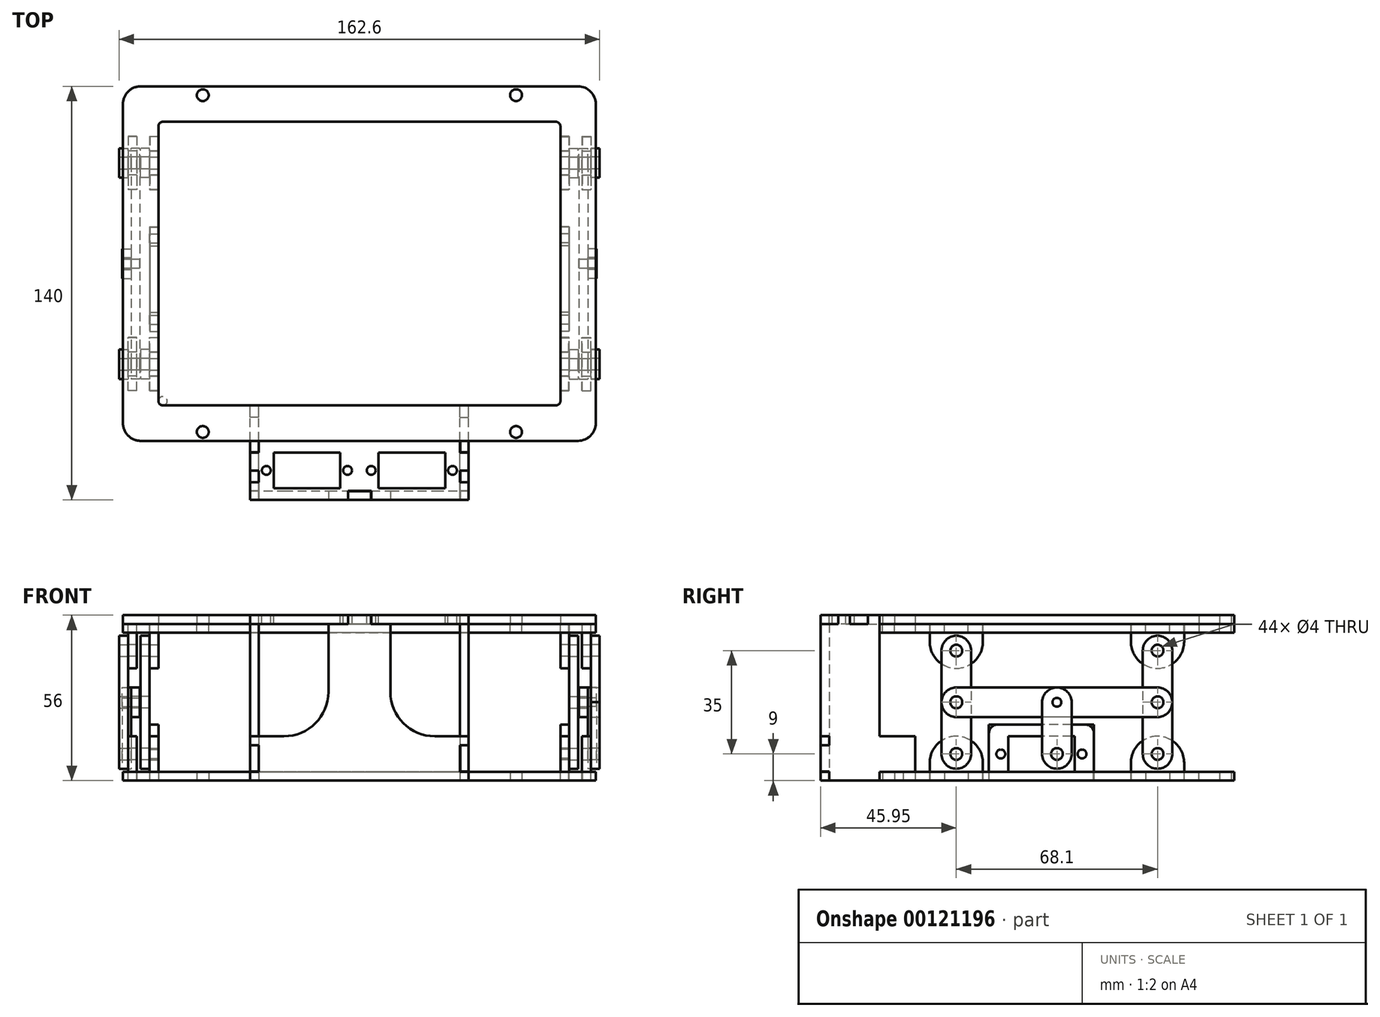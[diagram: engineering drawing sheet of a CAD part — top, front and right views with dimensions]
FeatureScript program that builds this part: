
annotation { "Feature Type Name" : "Feature", "Feature Type Description" : "" }
export const myFeature = defineFeature(function(context is Context, id is Id, definition is map)
    precondition{}
    {
        {
            var Q0;
            Q0=qCreatedBy(makeId("Top.planeOp"),FACE);
            var sketch = newSketch(context, id + "F0", { "sketchPlane" : qUnion([Q0])});
            skLineSegment(sketch, "E0.0.0", {"start": v(-163.03, 1.88) * mm, "end": v(-163.03, -118.12) * mm});
            skLineSegment(sketch, "E0.0.2", {"start": v(-163.03, -118.12) * mm, "end": v(-3.03, -118.12) * mm});
            skLineSegment(sketch, "E0.0.4", {"start": v(-3.03, -118.12) * mm, "end": v(-3.03, 1.88) * mm});
            skLineSegment(sketch, "E0.0.6", {"start": v(-3.03, 1.88) * mm, "end": v(-163.03, 1.88) * mm});
            skLineSegment(sketch, "E1.0", {"start": v(-151.03, -106.12) * mm, "end": v(-151.03, -10.12) * mm});
            skLineSegment(sketch, "E2.0", {"start": v(-151.03, -10.12) * mm, "end": v(-15.03, -10.12) * mm});
            skLineSegment(sketch, "E3.0", {"start": v(-15.03, -10.12) * mm, "end": v(-15.03, -106.12) * mm});
            skLineSegment(sketch, "E4.0", {"start": v(-15.03, -106.12) * mm, "end": v(-151.03, -106.12) * mm});
            skSolve(sketch);
        }
        {
            var Q0;
            Q0=qSketchRegion(id+"F0",true);
            extrude(context, id + "F1", {"entities" : qUnion([Q0]), "depth" : 3 * mm});
        }
        {
            var Q0;
            Q0=makeQuery(id+"F1.opExtrude","SWEPT_EDGE",EDGE,{"disambiguationData":[OSD([sQuery(id+"F0.wireOp",EDGE,"E0.0.0"),sQuery(id+"F0.wireOp",EDGE,"E0.0.2")])]});
            var Q1;
            Q1=makeQuery(id+"F1.opExtrude","SWEPT_EDGE",EDGE,{"disambiguationData":[OSD([sQuery(id+"F0.wireOp",EDGE,"E0.0.2"),sQuery(id+"F0.wireOp",EDGE,"E0.0.4")])]});
            var Q2;
            Q2=makeQuery(id+"F1.opExtrude","SWEPT_EDGE",EDGE,{"disambiguationData":[OSD([sQuery(id+"F0.wireOp",EDGE,"E0.0.0"),sQuery(id+"F0.wireOp",EDGE,"E0.0.6")])]});
            var Q3;
            Q3=makeQuery(id+"F1.opExtrude","SWEPT_EDGE",EDGE,{"disambiguationData":[OSD([sQuery(id+"F0.wireOp",EDGE,"E0.0.4"),sQuery(id+"F0.wireOp",EDGE,"E0.0.6")])]});
            fillet(context, id + "F2", {"entities" : qUnion([Q0, Q1, Q2, Q3]), "radius" : 6 * mm, "tangentPropagation" : true, "allowEdgeOverflow" : false});
        }
        {
            var Q0;
            Q0=makeQuery(id+"F1.opExtrude","SWEPT_EDGE",EDGE,{"disambiguationData":[OSD([sQuery(id+"F0.wireOp",EDGE,"E1.0"),sQuery(id+"F0.wireOp",EDGE,"E2.0")])]});
            var Q1;
            Q1=makeQuery(id+"F1.opExtrude","SWEPT_EDGE",EDGE,{"disambiguationData":[OSD([sQuery(id+"F0.wireOp",EDGE,"E2.0"),sQuery(id+"F0.wireOp",EDGE,"E3.0")])]});
            var Q2;
            Q2=makeQuery(id+"F1.opExtrude","SWEPT_EDGE",EDGE,{"disambiguationData":[OSD([sQuery(id+"F0.wireOp",EDGE,"E3.0"),sQuery(id+"F0.wireOp",EDGE,"E4.0")])]});
            var Q3;
            Q3=makeQuery(id+"F1.opExtrude","SWEPT_EDGE",EDGE,{"disambiguationData":[OSD([sQuery(id+"F0.wireOp",EDGE,"E1.0"),sQuery(id+"F0.wireOp",EDGE,"E4.0")])]});
            fillet(context, id + "F3", {"entities" : qUnion([Q0, Q1, Q2, Q3]), "radius" : 1.5 * mm, "tangentPropagation" : true, "allowEdgeOverflow" : false});
        }
        {
            var Q0;
            Q0=makeQuery(id+"F1.opExtrude","CAP_FACE",FACE,{"disambiguationData":[OSD([sQuery(id+"F0.wireOp",EDGE,"E0.0.0"),sQuery(id+"F0.wireOp",EDGE,"E0.0.2"),sQuery(id+"F0.wireOp",EDGE,"E0.0.4"),sQuery(id+"F0.wireOp",EDGE,"E0.0.6"),sQuery(id+"F0.wireOp",EDGE,"E1.0"),sQuery(id+"F0.wireOp",EDGE,"E2.0"),sQuery(id+"F0.wireOp",EDGE,"E3.0"),sQuery(id+"F0.wireOp",EDGE,"E4.0")])],"isStart":false});
            var sketch = newSketch(context, id + "F4", { "sketchPlane" : qUnion([Q0])});
            skLineSegment(sketch, "E5.bottom", {"start": v(-136.03, 1.88) * mm, "end": v(-30.03, 1.88) * mm, "construction": true});
            skLineSegment(sketch, "E5.top", {"start": v(-136.03, -118.12) * mm, "end": v(-30.03, -118.12) * mm, "construction": true});
            skLineSegment(sketch, "E5.left", {"start": v(-136.03, 1.88) * mm, "end": v(-136.03, -4.12) * mm, "construction": true});
            skLineSegment(sketch, "E5.right", {"start": v(-30.03, 1.88) * mm, "end": v(-30.03, -4.12) * mm, "construction": true});
            skLineSegment(sketch, "E6.trimOffspring", {"start": v(-136.03, -112.12) * mm, "end": v(-136.03, -118.12) * mm, "construction": true});
            skPoint(sketch, "E7.orphan", {"position": v(-149.53, -10.12) * mm});
            skLineSegment(sketch, "E8.trimOffspring", {"start": v(-30.03, -112.12) * mm, "end": v(-30.03, -118.12) * mm, "construction": true});
            skPoint(sketch, "E9.orphan", {"position": v(-16.53, -10.12) * mm});
            skPoint(sketch, "E10.orphan", {"position": v(-16.53, -106.12) * mm});
            skPoint(sketch, "E11.orphan", {"position": v(-149.53, -106.12) * mm});
            skLineSegment(sketch, "E12", {"start": v(-136.03, -4.12) * mm, "end": v(-30.03, -4.12) * mm, "construction": true});
            skLineSegment(sketch, "E13", {"start": v(-136.03, -112.12) * mm, "end": v(-30.03, -112.12) * mm, "construction": true});
            skPoint(sketch, "E14.0.end.orphan", {"position": v(-30.03, -10.12) * mm});
            skPoint(sketch, "E14.0.start.orphan", {"position": v(-136.03, -10.12) * mm});
            skPoint(sketch, "E15.orphan", {"position": v(-30.03, -106.12) * mm});
            skPoint(sketch, "E16.orphan", {"position": v(-136.03, -106.12) * mm});
            skCircle(sketch, "E17", {"center": v(-136.03, -1.12) * mm, "radius": 2 * mm});
            skCircle(sketch, "E18", {"center": v(-30.03, -1.12) * mm, "radius": 2 * mm});
            skCircle(sketch, "E19", {"center": v(-30.03, -115.12) * mm, "radius": 2 * mm});
            skCircle(sketch, "E20", {"center": v(-136.03, -115.12) * mm, "radius": 2 * mm});
            skSolve(sketch);
        }
        {
            var Q0;
            Q0=qSketchRegion(id+"F4",true);
            extrude(context, id + "F5", {"entities" : qUnion([Q0]), "operationType" : NewBodyOperationType.REMOVE, "endBound" : BoundingType.THROUGH_ALL, "oppositeDirection" : true, "depth" : 25 * mm});
        }
        {
            var Q0;
            Q0=makeQuery(id+"F1.opExtrude","CAP_FACE",FACE,{"disambiguationData":[OSD([sQuery(id+"F0.wireOp",EDGE,"E0.0.0"),sQuery(id+"F0.wireOp",EDGE,"E0.0.2"),sQuery(id+"F0.wireOp",EDGE,"E0.0.4"),sQuery(id+"F0.wireOp",EDGE,"E0.0.6"),sQuery(id+"F0.wireOp",EDGE,"E1.0"),sQuery(id+"F0.wireOp",EDGE,"E2.0"),sQuery(id+"F0.wireOp",EDGE,"E3.0"),sQuery(id+"F0.wireOp",EDGE,"E4.0")])],"isStart":false});
            var sketch = newSketch(context, id + "F6", { "sketchPlane" : qUnion([Q0])});
            skLineSegment(sketch, "E21.bottom", {"start": v(-151.03, -101.12) * mm, "end": v(-153.93, -101.12) * mm});
            skLineSegment(sketch, "E21.top", {"start": v(-151.03, -96.22) * mm, "end": v(-153.93, -96.22) * mm});
            skLineSegment(sketch, "E21.left", {"start": v(-151.03, -101.12) * mm, "end": v(-151.03, -96.22) * mm});
            skLineSegment(sketch, "E21.right", {"start": v(-153.93, -101.12) * mm, "end": v(-153.93, -96.22) * mm});
            skLineSegment(sketch, "E22.bottom", {"start": v(-151.03, -88.12) * mm, "end": v(-153.93, -88.12) * mm});
            skLineSegment(sketch, "E22.top", {"start": v(-151.03, -83.22) * mm, "end": v(-153.93, -83.22) * mm});
            skLineSegment(sketch, "E22.left", {"start": v(-151.03, -88.12) * mm, "end": v(-151.03, -83.22) * mm});
            skLineSegment(sketch, "E22.right", {"start": v(-153.93, -88.12) * mm, "end": v(-153.93, -83.22) * mm});
            skLineSegment(sketch, "E23.bottom", {"start": v(-158.43, -101.12) * mm, "end": v(-161.33, -101.12) * mm});
            skLineSegment(sketch, "E23.top", {"start": v(-158.43, -96.22) * mm, "end": v(-161.33, -96.22) * mm});
            skLineSegment(sketch, "E23.left", {"start": v(-158.43, -101.12) * mm, "end": v(-158.43, -96.22) * mm});
            skLineSegment(sketch, "E23.right", {"start": v(-161.33, -101.12) * mm, "end": v(-161.33, -96.22) * mm});
            skLineSegment(sketch, "E24.bottom", {"start": v(-158.43, -88.12) * mm, "end": v(-161.33, -88.12) * mm});
            skLineSegment(sketch, "E24.top", {"start": v(-158.43, -83.22) * mm, "end": v(-161.33, -83.22) * mm});
            skLineSegment(sketch, "E24.left", {"start": v(-158.43, -88.12) * mm, "end": v(-158.43, -83.22) * mm});
            skLineSegment(sketch, "E24.right", {"start": v(-161.33, -88.12) * mm, "end": v(-161.33, -83.22) * mm});
            skLineSegment(sketch, "E25", {"start": v(-163.03, -58.12) * mm, "end": v(-3.03, -58.12) * mm, "construction": true});
            skLineSegment(sketch, "E26", {"start": v(-83.03, 1.88) * mm, "end": v(-83.03, -118.12) * mm, "construction": true});
            skLineSegment(sketch, "E27.MirrorCS", {"start": v(-4.73, -101.12) * mm, "end": v(-4.73, -96.22) * mm});
            skLineSegment(sketch, "E28.MirrorCS", {"start": v(-7.63, -101.12) * mm, "end": v(-7.63, -96.22) * mm});
            skLineSegment(sketch, "E29.MirrorCS", {"start": v(-7.63, -96.22) * mm, "end": v(-4.73, -96.22) * mm});
            skLineSegment(sketch, "E30.MirrorCS", {"start": v(-7.63, -88.12) * mm, "end": v(-4.73, -88.12) * mm});
            skLineSegment(sketch, "E31.MirrorCS", {"start": v(-7.63, -101.12) * mm, "end": v(-4.73, -101.12) * mm});
            skLineSegment(sketch, "E32.MirrorCS", {"start": v(-12.13, -88.12) * mm, "end": v(-12.13, -83.22) * mm});
            skLineSegment(sketch, "E33.MirrorCS", {"start": v(-15.03, -88.12) * mm, "end": v(-15.03, -83.22) * mm});
            skLineSegment(sketch, "E34.MirrorCS", {"start": v(-15.03, -83.22) * mm, "end": v(-12.13, -83.22) * mm});
            skLineSegment(sketch, "E35.MirrorCS", {"start": v(-15.03, -88.12) * mm, "end": v(-12.13, -88.12) * mm});
            skLineSegment(sketch, "E36.MirrorCS", {"start": v(-12.13, -101.12) * mm, "end": v(-12.13, -96.22) * mm});
            skLineSegment(sketch, "E37.MirrorCS", {"start": v(-15.03, -101.12) * mm, "end": v(-15.03, -96.22) * mm});
            skLineSegment(sketch, "E38.MirrorCS", {"start": v(-7.63, -83.22) * mm, "end": v(-4.73, -83.22) * mm});
            skLineSegment(sketch, "E39.MirrorCS", {"start": v(-7.63, -88.12) * mm, "end": v(-7.63, -83.22) * mm});
            skLineSegment(sketch, "E40.MirrorCS", {"start": v(-15.03, -96.22) * mm, "end": v(-12.13, -96.22) * mm});
            skLineSegment(sketch, "E41.MirrorCS", {"start": v(-15.03, -101.12) * mm, "end": v(-12.13, -101.12) * mm});
            skLineSegment(sketch, "E42.MirrorCS", {"start": v(-4.73, -88.12) * mm, "end": v(-4.73, -83.22) * mm});
            skLineSegment(sketch, "E43.MirrorCS", {"start": v(-7.63, -15.12) * mm, "end": v(-4.73, -15.12) * mm});
            skLineSegment(sketch, "E44.MirrorCS", {"start": v(-153.93, -15.12) * mm, "end": v(-153.93, -20.02) * mm});
            skLineSegment(sketch, "E45.MirrorCS", {"start": v(-15.03, -20.02) * mm, "end": v(-12.13, -20.02) * mm});
            skLineSegment(sketch, "E46.MirrorCS", {"start": v(-161.33, -28.12) * mm, "end": v(-161.33, -33.02) * mm});
            skLineSegment(sketch, "E47.MirrorCS", {"start": v(-158.43, -20.02) * mm, "end": v(-161.33, -20.02) * mm});
            skLineSegment(sketch, "E48.MirrorCS", {"start": v(-15.03, -33.02) * mm, "end": v(-12.13, -33.02) * mm});
            skLineSegment(sketch, "E49.MirrorCS", {"start": v(-15.03, -28.12) * mm, "end": v(-12.13, -28.12) * mm});
            skLineSegment(sketch, "E50.MirrorCS", {"start": v(-158.43, -15.12) * mm, "end": v(-158.43, -20.02) * mm});
            skLineSegment(sketch, "E51.MirrorCS", {"start": v(-15.03, -15.12) * mm, "end": v(-15.03, -20.02) * mm});
            skLineSegment(sketch, "E52.MirrorCS", {"start": v(-4.73, -15.12) * mm, "end": v(-4.73, -20.02) * mm});
            skLineSegment(sketch, "E53.MirrorCS", {"start": v(-7.63, -15.12) * mm, "end": v(-7.63, -20.02) * mm});
            skLineSegment(sketch, "E54.MirrorCS", {"start": v(-151.03, -15.12) * mm, "end": v(-151.03, -20.02) * mm});
            skLineSegment(sketch, "E55.MirrorCS", {"start": v(-151.03, -15.12) * mm, "end": v(-153.93, -15.12) * mm});
            skLineSegment(sketch, "E56.MirrorCS", {"start": v(-15.03, -15.12) * mm, "end": v(-12.13, -15.12) * mm});
            skLineSegment(sketch, "E57.MirrorCS", {"start": v(-158.43, -15.12) * mm, "end": v(-161.33, -15.12) * mm});
            skLineSegment(sketch, "E58.MirrorCS", {"start": v(-12.13, -15.12) * mm, "end": v(-12.13, -20.02) * mm});
            skLineSegment(sketch, "E59.MirrorCS", {"start": v(-7.63, -33.02) * mm, "end": v(-4.73, -33.02) * mm});
            skLineSegment(sketch, "E60.MirrorCS", {"start": v(-153.93, -28.12) * mm, "end": v(-153.93, -33.02) * mm});
            skLineSegment(sketch, "E61.MirrorCS", {"start": v(-158.43, -28.12) * mm, "end": v(-158.43, -33.02) * mm});
            skLineSegment(sketch, "E62.MirrorCS", {"start": v(-15.03, -28.12) * mm, "end": v(-15.03, -33.02) * mm});
            skLineSegment(sketch, "E63.MirrorCS", {"start": v(-151.03, -33.02) * mm, "end": v(-153.93, -33.02) * mm});
            skLineSegment(sketch, "E64.MirrorCS", {"start": v(-151.03, -20.02) * mm, "end": v(-153.93, -20.02) * mm});
            skLineSegment(sketch, "E65.MirrorCS", {"start": v(-7.63, -20.02) * mm, "end": v(-4.73, -20.02) * mm});
            skLineSegment(sketch, "E66.MirrorCS", {"start": v(-7.63, -28.12) * mm, "end": v(-7.63, -33.02) * mm});
            skLineSegment(sketch, "E67.MirrorCS", {"start": v(-158.43, -28.12) * mm, "end": v(-161.33, -28.12) * mm});
            skLineSegment(sketch, "E68.MirrorCS", {"start": v(-4.73, -28.12) * mm, "end": v(-4.73, -33.02) * mm});
            skLineSegment(sketch, "E69.MirrorCS", {"start": v(-151.03, -28.12) * mm, "end": v(-153.93, -28.12) * mm});
            skLineSegment(sketch, "E70.MirrorCS", {"start": v(-151.03, -28.12) * mm, "end": v(-151.03, -33.02) * mm});
            skLineSegment(sketch, "E71.MirrorCS", {"start": v(-7.63, -28.12) * mm, "end": v(-4.73, -28.12) * mm});
            skLineSegment(sketch, "E72.MirrorCS", {"start": v(-158.43, -33.02) * mm, "end": v(-161.33, -33.02) * mm});
            skLineSegment(sketch, "E73.MirrorCS", {"start": v(-12.13, -28.12) * mm, "end": v(-12.13, -33.02) * mm});
            skLineSegment(sketch, "E74.MirrorCS", {"start": v(-161.33, -15.12) * mm, "end": v(-161.33, -20.02) * mm});
            skSolve(sketch);
        }
        {
            var Q0;
            Q0 = qSketchRegion(id + "F6", true);
            extrude(context, id + "F7", {"entities" : qUnion([Q0]), "operationType" : NewBodyOperationType.REMOVE, "endBound" : BoundingType.THROUGH_ALL, "oppositeDirection" : true, "depth" : 25 * mm});
        }
        {
            var Q0;
            Q0=makeQuery(id+"F1.opExtrude","CAP_FACE",FACE,{"disambiguationData":[OSD([sQuery(id+"F0.wireOp",EDGE,"E0.0.0"),sQuery(id+"F0.wireOp",EDGE,"E0.0.2"),sQuery(id+"F0.wireOp",EDGE,"E0.0.4"),sQuery(id+"F0.wireOp",EDGE,"E0.0.6"),sQuery(id+"F0.wireOp",EDGE,"E1.0"),sQuery(id+"F0.wireOp",EDGE,"E2.0"),sQuery(id+"F0.wireOp",EDGE,"E3.0"),sQuery(id+"F0.wireOp",EDGE,"E4.0")])],"isStart":false});
            var sketch = newSketch(context, id + "F8", { "sketchPlane" : qUnion([Q0])});
            skLineSegment(sketch, "E75.0", {"start": v(-9.03, 1.88) * mm, "end": v(-157.03, 1.88) * mm});
            skLineSegment(sketch, "E76.0", {"start": v(-163.03, -4.12) * mm, "end": v(-163.03, -112.12) * mm});
            skArc(sketch, "E77.0.1", {"start": v(-157.03, 1.88) * mm, "mid": v(-161.28, 0.12) * mm, "end": v(-163.03, -4.12) * mm});
            skArc(sketch, "E77.0.3", {"start": v(-163.03, -112.12) * mm, "mid": v(-161.28, -116.36) * mm, "end": v(-157.03, -118.12) * mm});
            skLineSegment(sketch, "E77.0.4", {"start": v(-157.03, -118.12) * mm, "end": v(-9.03, -118.12) * mm});
            skArc(sketch, "E77.0.5", {"start": v(-9.03, -118.12) * mm, "mid": v(-4.8, -116.36) * mm, "end": v(-3.03, -112.12) * mm});
            skLineSegment(sketch, "E77.0.6", {"start": v(-3.03, -112.12) * mm, "end": v(-3.03, -4.12) * mm});
            skArc(sketch, "E77.0.7", {"start": v(-3.03, -4.12) * mm, "mid": v(-4.8, 0.12) * mm, "end": v(-9.03, 1.88) * mm});
            skArc(sketch, "E78.0", {"start": v(-149.53, -106.12) * mm, "mid": v(-150.6, -105.68) * mm, "end": v(-151.03, -104.62) * mm});
            skLineSegment(sketch, "E79.0", {"start": v(-16.53, -106.12) * mm, "end": v(-149.53, -106.12) * mm});
            skArc(sketch, "E80.0", {"start": v(-151.03, -11.62) * mm, "mid": v(-150.6, -10.56) * mm, "end": v(-149.53, -10.12) * mm});
            skLineSegment(sketch, "E81.0", {"start": v(-149.53, -10.12) * mm, "end": v(-16.53, -10.12) * mm});
            skArc(sketch, "E82.0", {"start": v(-16.53, -10.12) * mm, "mid": v(-15.47, -10.56) * mm, "end": v(-15.03, -11.62) * mm});
            skArc(sketch, "E83.0", {"start": v(-15.03, -104.62) * mm, "mid": v(-15.47, -105.68) * mm, "end": v(-16.53, -106.12) * mm});
            skCircle(sketch, "E84.0", {"center": v(-30.03, -1.12) * mm, "radius": 2 * mm});
            skCircle(sketch, "E85.0", {"center": v(-136.03, -1.12) * mm, "radius": 2 * mm});
            skCircle(sketch, "E86.0", {"center": v(-30.03, -115.12) * mm, "radius": 2 * mm});
            skCircle(sketch, "E87.0", {"center": v(-136.03, -115.12) * mm, "radius": 2 * mm});
            skLineSegment(sketch, "E88", {"start": v(-151.03, -11.62) * mm, "end": v(-151.03, -104.62) * mm});
            skLineSegment(sketch, "E89", {"start": v(-15.03, -11.62) * mm, "end": v(-15.03, -104.62) * mm});
            skSolve(sketch);
        }
        {
            var Q0;
            Q0 = qSketchRegion(id + "F8", true);
            extrude(context, id + "F9", {"entities" : qUnion([Q0]), "depth" : 3 * mm});
        }
        {
            var Q0;
            {var subQ3=sQuery(id+"F0.wireOp",EDGE,"E1.0");Q0=makeQuery(id+"F7.boolean.opBoolean","SPLIT",FACE,{"disambiguationData":[TD([makeQuery(id+"F7.opExtrude","SWEPT_FACE",FACE,{"disambiguationData":[OSD([sQuery(id+"F6.wireOp",EDGE,"E21.top")])]})])],"derivedFrom":makeQuery(id+"F1.opExtrude","SWEPT_FACE",FACE,{"disambiguationData":[OSD([subQ3])]})});}
            var sketch = newSketch(context, id + "F10", { "sketchPlane" : qUnion([Q0])});
            skLineSegment(sketch, "E90.bottom", {"start": v(-101.17, 3) * mm, "end": v(-96.17, 3) * mm});
            skLineSegment(sketch, "E90.left", {"start": v(-101.17, 3) * mm, "end": v(-101.17, -3) * mm});
            skLineSegment(sketch, "E90.right", {"start": v(-83.17, 3) * mm, "end": v(-83.17, -3) * mm});
            skLineSegment(sketch, "E91.top", {"start": v(-96.17, 0) * mm, "end": v(-88.17, 0) * mm});
            skLineSegment(sketch, "E91.left", {"start": v(-96.17, 3) * mm, "end": v(-96.17, 0) * mm});
            skLineSegment(sketch, "E91.right", {"start": v(-88.17, 3) * mm, "end": v(-88.17, 0) * mm});
            skLineSegment(sketch, "E92", {"start": v(-92.17, 0) * mm, "end": v(-92.17, -12) * mm, "construction": true});
            skCircle(sketch, "E93", {"center": v(-92.17, -6) * mm, "radius": 2 * mm});
            skArc(sketch, "E94", {"start": v(-101.17, -3) * mm, "mid": v(-92.17, -12) * mm, "end": v(-83.17, -3) * mm});
            skPoint(sketch, "E94.first.point", {"position": v(-101.17, -3) * mm});
            skPoint(sketch, "E94.second.point", {"position": v(-83.17, -3) * mm});
            skPoint(sketch, "E94.third.point", {"position": v(-92.17, -12) * mm});
            skLineSegment(sketch, "E95.trimOffspring", {"start": v(-88.17, 3) * mm, "end": v(-83.17, 3) * mm});
            skLineSegment(sketch, "E96", {"start": v(-92.17, 3) * mm, "end": v(-92.17, 0) * mm, "construction": true});
            skSolve(sketch);
        }
        {
            var Q0;
            {var subQ8=sQuery(id+"F10.wireOp",EDGE,"E90.left");Q0=makeQuery(id+"F10.imprint","IMPRINT",FACE,{"disambiguationData":[TD([[makeQuery(id+"F10.imprint","IMPRINT",EDGE,{"derivedFrom":subQ8}),1.0]])]});}
            extrude(context, id + "F11", {"entities" : qUnion([Q0]), "oppositeDirection" : true, "depth" : 3 * mm});
        }
        {
            var Q0;
            {var subQ3=sQuery(id+"F0.wireOp",EDGE,"E1.0");Q0=makeQuery(id+"F7.boolean.opBoolean","SPLIT",FACE,{"disambiguationData":[TD([makeQuery(id+"F7.opExtrude","SWEPT_FACE",FACE,{"disambiguationData":[OSD([sQuery(id+"F6.wireOp",EDGE,"E22.top")])]})])],"derivedFrom":makeQuery(id+"F1.opExtrude","SWEPT_FACE",FACE,{"disambiguationData":[OSD([subQ3])]})});}
            var Q1;
            Q1=makeQuery(id+"F7.boolean.opBoolean","COPY",FACE,{"derivedFrom":makeQuery(id+"F7.opExtrude","SWEPT_FACE",FACE,{"disambiguationData":[OSD([sQuery(id+"F6.wireOp",EDGE,"E24.right")])]})});
            cPlane(context, id + "F12", {"entities" : qUnion([Q0, Q1]), "cplaneType" : CPlaneType.MID_PLANE, "offset" : 25 * mm, "width" : 150 * mm, "height" : 150 * mm});
        }
        {
            var Q0;
            Q0=makeQuery(id+"F11.opExtrude","SWEPT_BODY",BODY,{"disambiguationData":[OSD([sQuery(id+"F0.wireOp",EDGE,"E1.0"),sQuery(id+"F6.wireOp",EDGE,"E21.top"),sQuery(id+"F6.wireOp",EDGE,"E22.bottom"),sQuery(id+"F6.wireOp",EDGE,"E21.left"),sQuery(id+"F6.wireOp",EDGE,"E22.left"),sQuery(id+"F10.wireOp",EDGE,"E90.bottom"),sQuery(id+"F10.wireOp",EDGE,"E90.left"),sQuery(id+"F10.wireOp",EDGE,"E90.right"),sQuery(id+"F10.wireOp",EDGE,"E91.top"),sQuery(id+"F10.wireOp",EDGE,"E93"),sQuery(id+"F10.wireOp",EDGE,"E94"),sQuery(id+"F10.wireOp",EDGE,"E95.trimOffspring")])]});
            var Q1;
            Q1=qCreatedBy(id+"F12.planeOp",FACE);
            mirror(context, id + "F13", {"entities" : qUnion([Q0]), "mirrorPlane" : qUnion([Q1])});
        }
        {
            var Q0;
            Q0=makeQuery(id+"F1.opExtrude","SWEPT_FACE",FACE,{"disambiguationData":[OSD([sQuery(id+"F0.wireOp",EDGE,"E0.0.4")])]});
            var Q1;
            Q1=makeQuery(id+"F1.opExtrude","SWEPT_FACE",FACE,{"disambiguationData":[OSD([sQuery(id+"F0.wireOp",EDGE,"E0.0.0")])]});
            cPlane(context, id + "F14", {"entities" : qUnion([Q0, Q1]), "cplaneType" : CPlaneType.MID_PLANE, "offset" : 25 * mm, "width" : 150 * mm, "height" : 150 * mm});
        }
        {
            var Q0;
            Q0=makeQuery(id+"F1.opExtrude","SWEPT_FACE",FACE,{"disambiguationData":[OSD([sQuery(id+"F0.wireOp",EDGE,"E0.0.2")])]});
            var Q1;
            Q1=makeQuery(id+"F1.opExtrude","SWEPT_FACE",FACE,{"disambiguationData":[OSD([sQuery(id+"F0.wireOp",EDGE,"E0.0.6")])]});
            cPlane(context, id + "F15", {"entities" : qUnion([Q0, Q1]), "cplaneType" : CPlaneType.MID_PLANE, "offset" : 25 * mm, "width" : 150 * mm, "height" : 150 * mm});
        }
        {
            var Q0;
            Q0=makeQuery(id+"F11.opExtrude","SWEPT_BODY",BODY,{"disambiguationData":[OSD([sQuery(id+"F0.wireOp",EDGE,"E1.0"),sQuery(id+"F6.wireOp",EDGE,"E21.top"),sQuery(id+"F6.wireOp",EDGE,"E22.bottom"),sQuery(id+"F6.wireOp",EDGE,"E21.left"),sQuery(id+"F6.wireOp",EDGE,"E22.left"),sQuery(id+"F10.wireOp",EDGE,"E90.bottom"),sQuery(id+"F10.wireOp",EDGE,"E90.left"),sQuery(id+"F10.wireOp",EDGE,"E90.right"),sQuery(id+"F10.wireOp",EDGE,"E91.top"),sQuery(id+"F10.wireOp",EDGE,"E93"),sQuery(id+"F10.wireOp",EDGE,"E94"),sQuery(id+"F10.wireOp",EDGE,"E95.trimOffspring")])]});
            var Q1;
            Q1=makeQuery(id+"F13.opPattern","COPY",BODY,{"derivedFrom":makeQuery(id+"F11.opExtrude","SWEPT_BODY",BODY,{"disambiguationData":[OSD([sQuery(id+"F0.wireOp",EDGE,"E1.0"),sQuery(id+"F6.wireOp",EDGE,"E21.top"),sQuery(id+"F6.wireOp",EDGE,"E22.bottom"),sQuery(id+"F6.wireOp",EDGE,"E21.left"),sQuery(id+"F6.wireOp",EDGE,"E22.left"),sQuery(id+"F10.wireOp",EDGE,"E90.bottom"),sQuery(id+"F10.wireOp",EDGE,"E90.left"),sQuery(id+"F10.wireOp",EDGE,"E90.right"),sQuery(id+"F10.wireOp",EDGE,"E91.top"),sQuery(id+"F10.wireOp",EDGE,"E93"),sQuery(id+"F10.wireOp",EDGE,"E94"),sQuery(id+"F10.wireOp",EDGE,"E95.trimOffspring")])]}),"instanceName":"1"});
            var Q2;
            Q2=qCreatedBy(id+"F14.planeOp",FACE);
            mirror(context, id + "F16", {"entities" : qUnion([Q0, Q1]), "mirrorPlane" : qUnion([Q2])});
        }
        {
            var Q0;
            Q0=makeQuery(id+"F11.opExtrude","SWEPT_BODY",BODY,{"disambiguationData":[OSD([sQuery(id+"F0.wireOp",EDGE,"E1.0"),sQuery(id+"F6.wireOp",EDGE,"E21.top"),sQuery(id+"F6.wireOp",EDGE,"E22.bottom"),sQuery(id+"F6.wireOp",EDGE,"E21.left"),sQuery(id+"F6.wireOp",EDGE,"E22.left"),sQuery(id+"F10.wireOp",EDGE,"E90.bottom"),sQuery(id+"F10.wireOp",EDGE,"E90.left"),sQuery(id+"F10.wireOp",EDGE,"E90.right"),sQuery(id+"F10.wireOp",EDGE,"E91.top"),sQuery(id+"F10.wireOp",EDGE,"E93"),sQuery(id+"F10.wireOp",EDGE,"E94"),sQuery(id+"F10.wireOp",EDGE,"E95.trimOffspring")])]});
            var Q1;
            Q1=makeQuery(id+"F13.opPattern","COPY",BODY,{"derivedFrom":makeQuery(id+"F11.opExtrude","SWEPT_BODY",BODY,{"disambiguationData":[OSD([sQuery(id+"F0.wireOp",EDGE,"E1.0"),sQuery(id+"F6.wireOp",EDGE,"E21.top"),sQuery(id+"F6.wireOp",EDGE,"E22.bottom"),sQuery(id+"F6.wireOp",EDGE,"E21.left"),sQuery(id+"F6.wireOp",EDGE,"E22.left"),sQuery(id+"F10.wireOp",EDGE,"E90.bottom"),sQuery(id+"F10.wireOp",EDGE,"E90.left"),sQuery(id+"F10.wireOp",EDGE,"E90.right"),sQuery(id+"F10.wireOp",EDGE,"E91.top"),sQuery(id+"F10.wireOp",EDGE,"E93"),sQuery(id+"F10.wireOp",EDGE,"E94"),sQuery(id+"F10.wireOp",EDGE,"E95.trimOffspring")])]}),"instanceName":"1"});
            var Q2;
            Q2=makeQuery(id+"F16.opPattern","COPY",BODY,{"derivedFrom":makeQuery(id+"F11.opExtrude","SWEPT_BODY",BODY,{"disambiguationData":[OSD([sQuery(id+"F0.wireOp",EDGE,"E1.0"),sQuery(id+"F6.wireOp",EDGE,"E21.top"),sQuery(id+"F6.wireOp",EDGE,"E22.bottom"),sQuery(id+"F6.wireOp",EDGE,"E21.left"),sQuery(id+"F6.wireOp",EDGE,"E22.left"),sQuery(id+"F10.wireOp",EDGE,"E90.bottom"),sQuery(id+"F10.wireOp",EDGE,"E90.left"),sQuery(id+"F10.wireOp",EDGE,"E90.right"),sQuery(id+"F10.wireOp",EDGE,"E91.top"),sQuery(id+"F10.wireOp",EDGE,"E93"),sQuery(id+"F10.wireOp",EDGE,"E94"),sQuery(id+"F10.wireOp",EDGE,"E95.trimOffspring")])]}),"instanceName":"1"});
            var Q3;
            Q3=makeQuery(id+"F16.opPattern","COPY",BODY,{"derivedFrom":makeQuery(id+"F13.opPattern","COPY",BODY,{"derivedFrom":makeQuery(id+"F11.opExtrude","SWEPT_BODY",BODY,{"disambiguationData":[OSD([sQuery(id+"F0.wireOp",EDGE,"E1.0"),sQuery(id+"F6.wireOp",EDGE,"E21.top"),sQuery(id+"F6.wireOp",EDGE,"E22.bottom"),sQuery(id+"F6.wireOp",EDGE,"E21.left"),sQuery(id+"F6.wireOp",EDGE,"E22.left"),sQuery(id+"F10.wireOp",EDGE,"E90.bottom"),sQuery(id+"F10.wireOp",EDGE,"E90.left"),sQuery(id+"F10.wireOp",EDGE,"E90.right"),sQuery(id+"F10.wireOp",EDGE,"E91.top"),sQuery(id+"F10.wireOp",EDGE,"E93"),sQuery(id+"F10.wireOp",EDGE,"E94"),sQuery(id+"F10.wireOp",EDGE,"E95.trimOffspring")])]}),"instanceName":"1"}),"instanceName":"1"});
            var Q4;
            Q4=qCreatedBy(id+"F15.planeOp",FACE);
            mirror(context, id + "F17", {"entities" : qUnion([Q0, Q1, Q2, Q3]), "mirrorPlane" : qUnion([Q4])});
        }
        {
            var Q0;
            Q0=makeQuery(id+"F16.opPattern","COPY",FACE,{"derivedFrom":makeQuery(id+"F13.opPattern","COPY",FACE,{"derivedFrom":makeQuery(id+"F11.opExtrude","CAP_FACE",FACE,{"disambiguationData":[OSD([sQuery(id+"F0.wireOp",EDGE,"E1.0"),sQuery(id+"F6.wireOp",EDGE,"E21.top"),sQuery(id+"F6.wireOp",EDGE,"E22.bottom"),sQuery(id+"F6.wireOp",EDGE,"E21.left"),sQuery(id+"F6.wireOp",EDGE,"E22.left"),sQuery(id+"F10.wireOp",EDGE,"E90.bottom"),sQuery(id+"F10.wireOp",EDGE,"E90.left"),sQuery(id+"F10.wireOp",EDGE,"E90.right"),sQuery(id+"F10.wireOp",EDGE,"E91.top"),sQuery(id+"F10.wireOp",EDGE,"E93"),sQuery(id+"F10.wireOp",EDGE,"E94"),sQuery(id+"F10.wireOp",EDGE,"E95.trimOffspring")])],"isStart":true}),"instanceName":"1"}),"instanceName":"1"});
            var sketch = newSketch(context, id + "F18", { "sketchPlane" : qUnion([Q0])});
            skArc(sketch, "E97", {"start": v(-87.17, -6) * mm, "mid": v(-92.17, -1) * mm, "end": v(-97.17, -6) * mm});
            skCircle(sketch, "E98", {"center": v(-92.17, -6) * mm, "radius": 2 * mm});
            skLineSegment(sketch, "E99", {"start": v(-92.17, -6) * mm, "end": v(-92.17, -41) * mm, "construction": true});
            skLineSegment(sketch, "E100", {"start": v(-87.17, -6) * mm, "end": v(-87.17, -41) * mm});
            skLineSegment(sketch, "E101", {"start": v(-97.17, -6) * mm, "end": v(-97.17, -41) * mm});
            skCircle(sketch, "E102", {"center": v(-92.17, -41) * mm, "radius": 2 * mm});
            skCircle(sketch, "E103", {"center": v(-92.17, -23.5) * mm, "radius": 2 * mm});
            skArc(sketch, "E104", {"start": v(-97.17, -41) * mm, "mid": v(-92.17, -46) * mm, "end": v(-87.17, -41) * mm});
            skSolve(sketch);
        }
        {
            var Q0;
            Q0=makeQuery(id+"F18.imprint","IMPRINT",FACE,{"disambiguationData":[TD([[makeQuery(id+"F18.imprint","IMPRINT",EDGE,{"derivedFrom":sQuery(id+"F18.wireOp",EDGE,"E102")}),-1.0]])]});
            var Q1;
            {var subQ1=sQuery(id+"F18.wireOp",EDGE,"E97");Q1=makeQuery(id+"F18.imprint","IMPRINT",FACE,{"disambiguationData":[TD([[makeQuery(id+"F18.imprint","IMPRINT",EDGE,{"derivedFrom":subQ1}),1.0]])]});}
            extrude(context, id + "F19", {"entities" : qUnion([Q0, Q1]), "depth" : 3 * mm});
        }
        {
            var Q0;
            Q0=makeQuery(id+"F16.opPattern","COPY",FACE,{"derivedFrom":makeQuery(id+"F11.opExtrude","CAP_FACE",FACE,{"disambiguationData":[OSD([sQuery(id+"F0.wireOp",EDGE,"E1.0"),sQuery(id+"F6.wireOp",EDGE,"E21.top"),sQuery(id+"F6.wireOp",EDGE,"E22.bottom"),sQuery(id+"F6.wireOp",EDGE,"E21.left"),sQuery(id+"F6.wireOp",EDGE,"E22.left"),sQuery(id+"F10.wireOp",EDGE,"E90.bottom"),sQuery(id+"F10.wireOp",EDGE,"E90.left"),sQuery(id+"F10.wireOp",EDGE,"E90.right"),sQuery(id+"F10.wireOp",EDGE,"E91.top"),sQuery(id+"F10.wireOp",EDGE,"E93"),sQuery(id+"F10.wireOp",EDGE,"E94"),sQuery(id+"F10.wireOp",EDGE,"E95.trimOffspring")])],"isStart":false}),"instanceName":"1"});
            var Q1;
            Q1=makeQuery(id+"F19.opExtrude","CAP_FACE",FACE,{"disambiguationData":[OSD([sQuery(id+"F18.wireOp",EDGE,"E97"),sQuery(id+"F18.wireOp",EDGE,"E98"),sQuery(id+"F18.wireOp",EDGE,"E100"),sQuery(id+"F18.wireOp",EDGE,"E101"),sQuery(id+"F18.wireOp",EDGE,"E102"),sQuery(id+"F18.wireOp",EDGE,"E103"),sQuery(id+"F18.wireOp",EDGE,"E104")])],"isStart":false});
            cPlane(context, id + "F20", {"entities" : qUnion([Q0, Q1]), "cplaneType" : CPlaneType.MID_PLANE, "offset" : 25 * mm, "width" : 150 * mm, "height" : 150 * mm});
        }
        {
            var Q0;
            Q0=makeQuery(id+"F19.opExtrude","SWEPT_BODY",BODY,{"disambiguationData":[OSD([sQuery(id+"F18.wireOp",EDGE,"E97"),sQuery(id+"F18.wireOp",EDGE,"E98"),sQuery(id+"F18.wireOp",EDGE,"E100"),sQuery(id+"F18.wireOp",EDGE,"E101"),sQuery(id+"F18.wireOp",EDGE,"E102"),sQuery(id+"F18.wireOp",EDGE,"E103"),sQuery(id+"F18.wireOp",EDGE,"E104")])]});
            var Q1;
            Q1=qCreatedBy(id+"F20.planeOp",FACE);
            mirror(context, id + "F21", {"entities" : qUnion([Q0]), "mirrorPlane" : qUnion([Q1])});
        }
        {
            var Q0;
            Q0=makeQuery(id+"F19.opExtrude","SWEPT_BODY",BODY,{"disambiguationData":[OSD([sQuery(id+"F18.wireOp",EDGE,"E97"),sQuery(id+"F18.wireOp",EDGE,"E98"),sQuery(id+"F18.wireOp",EDGE,"E100"),sQuery(id+"F18.wireOp",EDGE,"E101"),sQuery(id+"F18.wireOp",EDGE,"E102"),sQuery(id+"F18.wireOp",EDGE,"E103"),sQuery(id+"F18.wireOp",EDGE,"E104")])]});
            var Q1;
            Q1=makeQuery(id+"F21.opPattern","COPY",BODY,{"derivedFrom":makeQuery(id+"F19.opExtrude","SWEPT_BODY",BODY,{"disambiguationData":[OSD([sQuery(id+"F18.wireOp",EDGE,"E97"),sQuery(id+"F18.wireOp",EDGE,"E98"),sQuery(id+"F18.wireOp",EDGE,"E100"),sQuery(id+"F18.wireOp",EDGE,"E101"),sQuery(id+"F18.wireOp",EDGE,"E102"),sQuery(id+"F18.wireOp",EDGE,"E103"),sQuery(id+"F18.wireOp",EDGE,"E104")])]}),"instanceName":"1"});
            var Q2;
            Q2=qCreatedBy(id+"F14.planeOp",FACE);
            mirror(context, id + "F22", {"entities" : qUnion([Q0, Q1]), "mirrorPlane" : qUnion([Q2])});
        }
        {
            var Q0;
            Q0=makeQuery(id+"F22.opPattern","COPY",BODY,{"derivedFrom":makeQuery(id+"F21.opPattern","COPY",BODY,{"derivedFrom":makeQuery(id+"F19.opExtrude","SWEPT_BODY",BODY,{"disambiguationData":[OSD([sQuery(id+"F18.wireOp",EDGE,"E97"),sQuery(id+"F18.wireOp",EDGE,"E98"),sQuery(id+"F18.wireOp",EDGE,"E100"),sQuery(id+"F18.wireOp",EDGE,"E101"),sQuery(id+"F18.wireOp",EDGE,"E102"),sQuery(id+"F18.wireOp",EDGE,"E103"),sQuery(id+"F18.wireOp",EDGE,"E104")])]}),"instanceName":"1"}),"instanceName":"1"});
            var Q1;
            Q1=makeQuery(id+"F19.opExtrude","SWEPT_BODY",BODY,{"disambiguationData":[OSD([sQuery(id+"F18.wireOp",EDGE,"E97"),sQuery(id+"F18.wireOp",EDGE,"E98"),sQuery(id+"F18.wireOp",EDGE,"E100"),sQuery(id+"F18.wireOp",EDGE,"E101"),sQuery(id+"F18.wireOp",EDGE,"E102"),sQuery(id+"F18.wireOp",EDGE,"E103"),sQuery(id+"F18.wireOp",EDGE,"E104")])]});
            var Q2;
            Q2=makeQuery(id+"F22.opPattern","COPY",BODY,{"derivedFrom":makeQuery(id+"F19.opExtrude","SWEPT_BODY",BODY,{"disambiguationData":[OSD([sQuery(id+"F18.wireOp",EDGE,"E97"),sQuery(id+"F18.wireOp",EDGE,"E98"),sQuery(id+"F18.wireOp",EDGE,"E100"),sQuery(id+"F18.wireOp",EDGE,"E101"),sQuery(id+"F18.wireOp",EDGE,"E102"),sQuery(id+"F18.wireOp",EDGE,"E103"),sQuery(id+"F18.wireOp",EDGE,"E104")])]}),"instanceName":"1"});
            var Q3;
            Q3=makeQuery(id+"F21.opPattern","COPY",BODY,{"derivedFrom":makeQuery(id+"F19.opExtrude","SWEPT_BODY",BODY,{"disambiguationData":[OSD([sQuery(id+"F18.wireOp",EDGE,"E97"),sQuery(id+"F18.wireOp",EDGE,"E98"),sQuery(id+"F18.wireOp",EDGE,"E100"),sQuery(id+"F18.wireOp",EDGE,"E101"),sQuery(id+"F18.wireOp",EDGE,"E102"),sQuery(id+"F18.wireOp",EDGE,"E103"),sQuery(id+"F18.wireOp",EDGE,"E104")])]}),"instanceName":"1"});
            var Q4;
            Q4=qCreatedBy(id+"F15.planeOp",FACE);
            mirror(context, id + "F23", {"entities" : qUnion([Q0, Q1, Q2, Q3]), "mirrorPlane" : qUnion([Q4])});
        }
        {
            var Q0;
            Q0=makeQuery(id+"F19.opExtrude","CAP_FACE",FACE,{"disambiguationData":[OSD([sQuery(id+"F18.wireOp",EDGE,"E97"),sQuery(id+"F18.wireOp",EDGE,"E98"),sQuery(id+"F18.wireOp",EDGE,"E100"),sQuery(id+"F18.wireOp",EDGE,"E101"),sQuery(id+"F18.wireOp",EDGE,"E102"),sQuery(id+"F18.wireOp",EDGE,"E103"),sQuery(id+"F18.wireOp",EDGE,"E104")])],"isStart":false});
            var sketch = newSketch(context, id + "F24", { "sketchPlane" : qUnion([Q0])});
            skCircle(sketch, "E105.0", {"center": v(-24.07, -23.5) * mm, "radius": 2 * mm});
            skLineSegment(sketch, "E106", {"start": v(-24.07, -23.5) * mm, "end": v(-92.17, -23.5) * mm, "construction": true});
            skCircle(sketch, "E107", {"center": v(-92.17, -23.5) * mm, "radius": 2 * mm});
            skArc(sketch, "E108.0.startCap", {"start": v(-24.07, -18.5) * mm, "mid": v(-19.07, -23.5) * mm, "end": v(-24.07, -28.5) * mm});
            skArc(sketch, "E108.0.endCap", {"start": v(-92.17, -28.5) * mm, "mid": v(-97.17, -23.5) * mm, "end": v(-92.17, -18.5) * mm});
            skLineSegment(sketch, "E108.0.left", {"start": v(-24.07, -28.5) * mm, "end": v(-92.17, -28.5) * mm});
            skLineSegment(sketch, "E108.0.right", {"start": v(-24.07, -18.5) * mm, "end": v(-92.17, -18.5) * mm});
            skSolve(sketch);
        }
        {
            var Q0;
            Q0 = qSketchRegion(id + "F24", true);
            extrude(context, id + "F25", {"entities" : qUnion([Q0]), "oppositeDirection" : true, "depth" : 7 * mm});
        }
        {
            var Q0;
            Q0 = qSketchRegion(id + "F24", true);
            extrude(context, id + "F26", {"entities" : qUnion([Q0]), "operationType" : NewBodyOperationType.REMOVE, "oppositeDirection" : true, "depth" : 4 * mm});
        }
        {
            var Q0;
            Q0=makeQuery(id+"F25.opExtrude","SWEPT_BODY",BODY,{"disambiguationData":[OSD([sQuery(id+"F24.wireOp",EDGE,"E105.0"),sQuery(id+"F24.wireOp",EDGE,"E107"),sQuery(id+"F24.wireOp",EDGE,"E108.0.startCap"),sQuery(id+"F24.wireOp",EDGE,"E108.0.endCap"),sQuery(id+"F24.wireOp",EDGE,"E108.0.left"),sQuery(id+"F24.wireOp",EDGE,"E108.0.right")])]});
            var Q1;
            Q1=qCreatedBy(id+"F14.planeOp",FACE);
            mirror(context, id + "F27", {"entities" : qUnion([Q0]), "mirrorPlane" : qUnion([Q1])});
        }
        {
            var Q0;
            Q0=makeQuery(id+"F27.opPattern","COPY",FACE,{"derivedFrom":makeQuery(id+"F25.opExtrude","SWEPT_FACE",FACE,{"disambiguationData":[OSD([sQuery(id+"F24.wireOp",EDGE,"E108.0.right")])]}),"instanceName":"1"});
            var Q1;
            Q1=makeQuery(id+"F27.opPattern","COPY",FACE,{"derivedFrom":makeQuery(id+"F25.opExtrude","SWEPT_FACE",FACE,{"disambiguationData":[OSD([sQuery(id+"F24.wireOp",EDGE,"E108.0.left")])]}),"instanceName":"1"});
            cPlane(context, id + "F28", {"entities" : qUnion([Q0, Q1]), "cplaneType" : CPlaneType.MID_PLANE, "offset" : 25 * mm, "width" : 150 * mm, "height" : 150 * mm});
        }
        {
            var Q0;
            Q0=makeQuery(id+"F17.opPattern","COPY",BODY,{"derivedFrom":makeQuery(id+"F13.opPattern","COPY",BODY,{"derivedFrom":makeQuery(id+"F11.opExtrude","SWEPT_BODY",BODY,{"disambiguationData":[OSD([sQuery(id+"F0.wireOp",EDGE,"E1.0"),sQuery(id+"F6.wireOp",EDGE,"E21.top"),sQuery(id+"F6.wireOp",EDGE,"E22.bottom"),sQuery(id+"F6.wireOp",EDGE,"E21.left"),sQuery(id+"F6.wireOp",EDGE,"E22.left"),sQuery(id+"F10.wireOp",EDGE,"E90.bottom"),sQuery(id+"F10.wireOp",EDGE,"E90.left"),sQuery(id+"F10.wireOp",EDGE,"E90.right"),sQuery(id+"F10.wireOp",EDGE,"E91.top"),sQuery(id+"F10.wireOp",EDGE,"E93"),sQuery(id+"F10.wireOp",EDGE,"E94"),sQuery(id+"F10.wireOp",EDGE,"E95.trimOffspring")])]}),"instanceName":"1"}),"instanceName":"1"});
            var Q1;
            Q1=makeQuery(id+"F13.opPattern","COPY",BODY,{"derivedFrom":makeQuery(id+"F11.opExtrude","SWEPT_BODY",BODY,{"disambiguationData":[OSD([sQuery(id+"F0.wireOp",EDGE,"E1.0"),sQuery(id+"F6.wireOp",EDGE,"E21.top"),sQuery(id+"F6.wireOp",EDGE,"E22.bottom"),sQuery(id+"F6.wireOp",EDGE,"E21.left"),sQuery(id+"F6.wireOp",EDGE,"E22.left"),sQuery(id+"F10.wireOp",EDGE,"E90.bottom"),sQuery(id+"F10.wireOp",EDGE,"E90.left"),sQuery(id+"F10.wireOp",EDGE,"E90.right"),sQuery(id+"F10.wireOp",EDGE,"E91.top"),sQuery(id+"F10.wireOp",EDGE,"E93"),sQuery(id+"F10.wireOp",EDGE,"E94"),sQuery(id+"F10.wireOp",EDGE,"E95.trimOffspring")])]}),"instanceName":"1"});
            var Q2;
            Q2=makeQuery(id+"F16.opPattern","COPY",BODY,{"derivedFrom":makeQuery(id+"F13.opPattern","COPY",BODY,{"derivedFrom":makeQuery(id+"F11.opExtrude","SWEPT_BODY",BODY,{"disambiguationData":[OSD([sQuery(id+"F0.wireOp",EDGE,"E1.0"),sQuery(id+"F6.wireOp",EDGE,"E21.top"),sQuery(id+"F6.wireOp",EDGE,"E22.bottom"),sQuery(id+"F6.wireOp",EDGE,"E21.left"),sQuery(id+"F6.wireOp",EDGE,"E22.left"),sQuery(id+"F10.wireOp",EDGE,"E90.bottom"),sQuery(id+"F10.wireOp",EDGE,"E90.left"),sQuery(id+"F10.wireOp",EDGE,"E90.right"),sQuery(id+"F10.wireOp",EDGE,"E91.top"),sQuery(id+"F10.wireOp",EDGE,"E93"),sQuery(id+"F10.wireOp",EDGE,"E94"),sQuery(id+"F10.wireOp",EDGE,"E95.trimOffspring")])]}),"instanceName":"1"}),"instanceName":"1"});
            var Q3;
            Q3=makeQuery(id+"F17.opPattern","COPY",BODY,{"derivedFrom":makeQuery(id+"F16.opPattern","COPY",BODY,{"derivedFrom":makeQuery(id+"F13.opPattern","COPY",BODY,{"derivedFrom":makeQuery(id+"F11.opExtrude","SWEPT_BODY",BODY,{"disambiguationData":[OSD([sQuery(id+"F0.wireOp",EDGE,"E1.0"),sQuery(id+"F6.wireOp",EDGE,"E21.top"),sQuery(id+"F6.wireOp",EDGE,"E22.bottom"),sQuery(id+"F6.wireOp",EDGE,"E21.left"),sQuery(id+"F6.wireOp",EDGE,"E22.left"),sQuery(id+"F10.wireOp",EDGE,"E90.bottom"),sQuery(id+"F10.wireOp",EDGE,"E90.left"),sQuery(id+"F10.wireOp",EDGE,"E90.right"),sQuery(id+"F10.wireOp",EDGE,"E91.top"),sQuery(id+"F10.wireOp",EDGE,"E93"),sQuery(id+"F10.wireOp",EDGE,"E94"),sQuery(id+"F10.wireOp",EDGE,"E95.trimOffspring")])]}),"instanceName":"1"}),"instanceName":"1"}),"instanceName":"1"});
            var Q4;
            Q4=makeQuery(id+"F1.opExtrude","SWEPT_BODY",BODY,{"disambiguationData":[OSD([sQuery(id+"F0.wireOp",EDGE,"E0.0.0"),sQuery(id+"F0.wireOp",EDGE,"E0.0.2"),sQuery(id+"F0.wireOp",EDGE,"E0.0.4"),sQuery(id+"F0.wireOp",EDGE,"E0.0.6"),sQuery(id+"F0.wireOp",EDGE,"E1.0"),sQuery(id+"F0.wireOp",EDGE,"E2.0"),sQuery(id+"F0.wireOp",EDGE,"E3.0"),sQuery(id+"F0.wireOp",EDGE,"E4.0")])]});
            var Q5;
            Q5=makeQuery(id+"F11.opExtrude","SWEPT_BODY",BODY,{"disambiguationData":[OSD([sQuery(id+"F0.wireOp",EDGE,"E1.0"),sQuery(id+"F6.wireOp",EDGE,"E21.top"),sQuery(id+"F6.wireOp",EDGE,"E22.bottom"),sQuery(id+"F6.wireOp",EDGE,"E21.left"),sQuery(id+"F6.wireOp",EDGE,"E22.left"),sQuery(id+"F10.wireOp",EDGE,"E90.bottom"),sQuery(id+"F10.wireOp",EDGE,"E90.left"),sQuery(id+"F10.wireOp",EDGE,"E90.right"),sQuery(id+"F10.wireOp",EDGE,"E91.top"),sQuery(id+"F10.wireOp",EDGE,"E93"),sQuery(id+"F10.wireOp",EDGE,"E94"),sQuery(id+"F10.wireOp",EDGE,"E95.trimOffspring")])]});
            var Q6;
            Q6=makeQuery(id+"F17.opPattern","COPY",BODY,{"derivedFrom":makeQuery(id+"F11.opExtrude","SWEPT_BODY",BODY,{"disambiguationData":[OSD([sQuery(id+"F0.wireOp",EDGE,"E1.0"),sQuery(id+"F6.wireOp",EDGE,"E21.top"),sQuery(id+"F6.wireOp",EDGE,"E22.bottom"),sQuery(id+"F6.wireOp",EDGE,"E21.left"),sQuery(id+"F6.wireOp",EDGE,"E22.left"),sQuery(id+"F10.wireOp",EDGE,"E90.bottom"),sQuery(id+"F10.wireOp",EDGE,"E90.left"),sQuery(id+"F10.wireOp",EDGE,"E90.right"),sQuery(id+"F10.wireOp",EDGE,"E91.top"),sQuery(id+"F10.wireOp",EDGE,"E93"),sQuery(id+"F10.wireOp",EDGE,"E94"),sQuery(id+"F10.wireOp",EDGE,"E95.trimOffspring")])]}),"instanceName":"1"});
            var Q7;
            Q7=makeQuery(id+"F17.opPattern","COPY",BODY,{"derivedFrom":makeQuery(id+"F16.opPattern","COPY",BODY,{"derivedFrom":makeQuery(id+"F11.opExtrude","SWEPT_BODY",BODY,{"disambiguationData":[OSD([sQuery(id+"F0.wireOp",EDGE,"E1.0"),sQuery(id+"F6.wireOp",EDGE,"E21.top"),sQuery(id+"F6.wireOp",EDGE,"E22.bottom"),sQuery(id+"F6.wireOp",EDGE,"E21.left"),sQuery(id+"F6.wireOp",EDGE,"E22.left"),sQuery(id+"F10.wireOp",EDGE,"E90.bottom"),sQuery(id+"F10.wireOp",EDGE,"E90.left"),sQuery(id+"F10.wireOp",EDGE,"E90.right"),sQuery(id+"F10.wireOp",EDGE,"E91.top"),sQuery(id+"F10.wireOp",EDGE,"E93"),sQuery(id+"F10.wireOp",EDGE,"E94"),sQuery(id+"F10.wireOp",EDGE,"E95.trimOffspring")])]}),"instanceName":"1"}),"instanceName":"1"});
            var Q8;
            Q8=makeQuery(id+"F16.opPattern","COPY",BODY,{"derivedFrom":makeQuery(id+"F11.opExtrude","SWEPT_BODY",BODY,{"disambiguationData":[OSD([sQuery(id+"F0.wireOp",EDGE,"E1.0"),sQuery(id+"F6.wireOp",EDGE,"E21.top"),sQuery(id+"F6.wireOp",EDGE,"E22.bottom"),sQuery(id+"F6.wireOp",EDGE,"E21.left"),sQuery(id+"F6.wireOp",EDGE,"E22.left"),sQuery(id+"F10.wireOp",EDGE,"E90.bottom"),sQuery(id+"F10.wireOp",EDGE,"E90.left"),sQuery(id+"F10.wireOp",EDGE,"E90.right"),sQuery(id+"F10.wireOp",EDGE,"E91.top"),sQuery(id+"F10.wireOp",EDGE,"E93"),sQuery(id+"F10.wireOp",EDGE,"E94"),sQuery(id+"F10.wireOp",EDGE,"E95.trimOffspring")])]}),"instanceName":"1"});
            var Q9;
            Q9=qCreatedBy(id+"F28.planeOp",FACE);
            mirror(context, id + "F29", {"entities" : qUnion([Q0, Q1, Q2, Q3, Q4, Q5, Q6, Q7, Q8]), "mirrorPlane" : qUnion([Q9])});
        }
        {
            var Q0;
            Q0=makeQuery(id+"F26.boolean.opBoolean","COPY",FACE,{"derivedFrom":makeQuery(id+"F26.opExtrude","CAP_FACE",FACE,{"disambiguationData":[OSD([sQuery(id+"F24.wireOp",EDGE,"E105.0"),sQuery(id+"F24.wireOp",EDGE,"E107"),sQuery(id+"F24.wireOp",EDGE,"E108.0.startCap"),sQuery(id+"F24.wireOp",EDGE,"E108.0.endCap"),sQuery(id+"F24.wireOp",EDGE,"E108.0.left"),sQuery(id+"F24.wireOp",EDGE,"E108.0.right")])],"isStart":false})});
            var sketch = newSketch(context, id + "F30", { "sketchPlane" : qUnion([Q0])});
            skLineSegment(sketch, "E109", {"start": v(-97.17, -23.5) * mm, "end": v(-19.07, -23.5) * mm, "construction": true});
            skCircle(sketch, "E110", {"center": v(-58.12, -23.5) * mm, "radius": 1.5 * mm});
            skSolve(sketch);
        }
        {
            var Q0;
            Q0 = qSketchRegion(id + "F30", true);
            var Q1;
            Q1=makeQuery(id+"F25.opExtrude","SWEPT_BODY",BODY,{"disambiguationData":[OSD([sQuery(id+"F24.wireOp",EDGE,"E105.0"),sQuery(id+"F24.wireOp",EDGE,"E107"),sQuery(id+"F24.wireOp",EDGE,"E108.0.startCap"),sQuery(id+"F24.wireOp",EDGE,"E108.0.endCap"),sQuery(id+"F24.wireOp",EDGE,"E108.0.left"),sQuery(id+"F24.wireOp",EDGE,"E108.0.right")])]});
            extrude(context, id + "F31", {"entities" : qUnion([Q0]), "operationType" : NewBodyOperationType.REMOVE, "endBound" : BoundingType.THROUGH_ALL, "oppositeDirection" : true, "endBoundEntityBody" : qUnion([Q1]), "depth" : 25 * mm});
        }
        {
            var Q0;
            {var subQ1=sQuery(id+"F0.wireOp",EDGE,"E3.0");Q0=makeQuery(id+"F29.opPattern","COPY",FACE,{"derivedFrom":makeQuery(id+"F7.boolean.opBoolean","SPLIT",FACE,{"disambiguationData":[TD([makeQuery(id+"F7.opExtrude","SWEPT_FACE",FACE,{"disambiguationData":[OSD([sQuery(id+"F6.wireOp",EDGE,"E34.MirrorCS")])]})])],"derivedFrom":makeQuery(id+"F1.opExtrude","SWEPT_FACE",FACE,{"disambiguationData":[OSD([subQ1])]})}),"instanceName":"1"});}
            var sketch = newSketch(context, id + "F32", { "sketchPlane" : qUnion([Q0])});
            skLineSegment(sketch, "E111", {"start": v(58.12, -50) * mm, "end": v(58.12, -13.96) * mm, "construction": true});
            skLineSegment(sketch, "E112", {"start": v(49.62, -41) * mm, "end": v(77.12, -41) * mm, "construction": true});
            skLineSegment(sketch, "E113.bottom", {"start": v(52.12, -35) * mm, "end": v(74.62, -35) * mm});
            skLineSegment(sketch, "E113.top", {"start": v(52.12, -47) * mm, "end": v(74.62, -47) * mm});
            skLineSegment(sketch, "E113.left", {"start": v(52.12, -35) * mm, "end": v(52.12, -47) * mm});
            skLineSegment(sketch, "E113.right", {"start": v(74.62, -35) * mm, "end": v(74.62, -47) * mm});
            skCircle(sketch, "E114", {"center": v(49.62, -41) * mm, "radius": 1.5 * mm});
            skCircle(sketch, "E115", {"center": v(77.12, -41) * mm, "radius": 1.5 * mm});
            skCircle(sketch, "E116", {"center": v(58.12, -41) * mm, "radius": 6 * mm, "construction": true});
            skPoint(sketch, "E116.first.point", {"position": v(58.12, -35) * mm});
            skPoint(sketch, "E116.second.point", {"position": v(52.12, -41) * mm});
            skPoint(sketch, "E116.third.point", {"position": v(58.12, -47) * mm});
            skLineSegment(sketch, "E117", {"start": v(58.12, -41) * mm, "end": v(58.12, -35) * mm, "construction": true});
            skLineSegment(sketch, "E118.bottom", {"start": v(45.62, -31) * mm, "end": v(81.12, -31) * mm});
            skLineSegment(sketch, "E118.top", {"start": v(45.62, -50) * mm, "end": v(81.12, -50) * mm});
            skLineSegment(sketch, "E118.left", {"start": v(45.62, -31) * mm, "end": v(45.62, -50) * mm});
            skLineSegment(sketch, "E118.right", {"start": v(81.12, -31) * mm, "end": v(81.12, -50) * mm});
            skSolve(sketch);
        }
        {
            var Q0;
            Q0 = qSketchRegion(id + "F32", true);
            extrude(context, id + "F33", {"entities" : qUnion([Q0]), "oppositeDirection" : true, "depth" : 3 * mm});
        }
        {
            var Q0;
            {var subQ1=sQuery(id+"F0.wireOp",EDGE,"E3.0");Q0=makeQuery(id+"F29.opPattern","COPY",FACE,{"derivedFrom":makeQuery(id+"F7.boolean.opBoolean","SPLIT",FACE,{"disambiguationData":[TD([makeQuery(id+"F7.opExtrude","SWEPT_FACE",FACE,{"disambiguationData":[OSD([sQuery(id+"F6.wireOp",EDGE,"E34.MirrorCS")])]})])],"derivedFrom":makeQuery(id+"F1.opExtrude","SWEPT_FACE",FACE,{"disambiguationData":[OSD([subQ1])]})}),"instanceName":"1"});}
            var sketch = newSketch(context, id + "F34", { "sketchPlane" : qUnion([Q0])});
            skLineSegment(sketch, "E119.0", {"start": v(52.12, -35) * mm, "end": v(74.62, -35) * mm, "construction": true});
            skLineSegment(sketch, "E120", {"start": v(63.37, -35) * mm, "end": v(63.37, -50) * mm, "construction": true});
            skLineSegment(sketch, "E121.bottom", {"start": v(45.72, -50) * mm, "end": v(81.02, -50) * mm});
            skLineSegment(sketch, "E121.top", {"start": v(45.72, -47) * mm, "end": v(81.02, -47) * mm});
            skLineSegment(sketch, "E121.left", {"start": v(45.72, -50) * mm, "end": v(45.72, -47) * mm});
            skLineSegment(sketch, "E121.right", {"start": v(81.02, -50) * mm, "end": v(81.02, -47) * mm});
            skLineSegment(sketch, "E122", {"start": v(63.37, -47) * mm, "end": v(63.37, -50) * mm, "construction": true});
            skSolve(sketch);
        }
        {
            var Q0;
            Q0 = qSketchRegion(id + "F34", true);
            extrude(context, id + "F35", {"entities" : qUnion([Q0]), "operationType" : NewBodyOperationType.REMOVE, "oppositeDirection" : true, "depth" : 2.9 * mm, "hasSecondDirection" : true, "secondDirectionOppositeDirection" : false, "secondDirectionDepth" : (136 + 2.9) * mm});
        }
        {
            var Q0;
            Q0=makeQuery(id+"F26.boolean.opBoolean","COPY",FACE,{"derivedFrom":makeQuery(id+"F26.opExtrude","CAP_FACE",FACE,{"disambiguationData":[OSD([sQuery(id+"F24.wireOp",EDGE,"E105.0"),sQuery(id+"F24.wireOp",EDGE,"E107"),sQuery(id+"F24.wireOp",EDGE,"E108.0.startCap"),sQuery(id+"F24.wireOp",EDGE,"E108.0.endCap"),sQuery(id+"F24.wireOp",EDGE,"E108.0.left"),sQuery(id+"F24.wireOp",EDGE,"E108.0.right")])],"isStart":false})});
            var sketch = newSketch(context, id + "F36", { "sketchPlane" : qUnion([Q0])});
            skCircle(sketch, "E123.0", {"center": v(-58.12, -23.5) * mm, "radius": 1.5 * mm});
            skCircle(sketch, "E124.0", {"center": v(-49.62, -41) * mm, "radius": 1.5 * mm, "construction": true});
            skCircle(sketch, "E125.0", {"center": v(-77.12, -41) * mm, "radius": 1.5 * mm, "construction": true});
            skLineSegment(sketch, "E126", {"start": v(-77.12, -41) * mm, "end": v(-49.62, -41) * mm, "construction": true});
            skLineSegment(sketch, "E127", {"start": v(-58.12, -23.5) * mm, "end": v(-58.12, -41) * mm, "construction": true});
            skArc(sketch, "E128.0.startCap", {"start": v(-63.12, -23.5) * mm, "mid": v(-58.12, -18.5) * mm, "end": v(-53.12, -23.5) * mm});
            skArc(sketch, "E128.0.endCap", {"start": v(-53.12, -41) * mm, "mid": v(-58.12, -46) * mm, "end": v(-63.12, -41) * mm});
            skLineSegment(sketch, "E128.0.left", {"start": v(-53.12, -23.5) * mm, "end": v(-53.12, -41) * mm});
            skLineSegment(sketch, "E128.0.right", {"start": v(-63.12, -23.5) * mm, "end": v(-63.12, -41) * mm});
            skCircle(sketch, "E129", {"center": v(-58.12, -41) * mm, "radius": 2 * mm});
            skSolve(sketch);
        }
        {
            var Q0;
            Q0 = qSketchRegion(id + "F36", true);
            extrude(context, id + "F37", {"entities" : qUnion([Q0]), "depth" : 3 * mm});
        }
        {
            var Q0;
            Q0=makeQuery(id+"F9.opExtrude","CAP_FACE",FACE,{"disambiguationData":[OSD([sQuery(id+"F8.wireOp",EDGE,"E75.0"),sQuery(id+"F8.wireOp",EDGE,"E77.0.1"),sQuery(id+"F8.wireOp",EDGE,"E76.0"),sQuery(id+"F8.wireOp",EDGE,"E77.0.3"),sQuery(id+"F8.wireOp",EDGE,"E77.0.4"),sQuery(id+"F8.wireOp",EDGE,"E77.0.5"),sQuery(id+"F8.wireOp",EDGE,"E77.0.6"),sQuery(id+"F8.wireOp",EDGE,"E77.0.7"),sQuery(id+"F8.wireOp",EDGE,"E78.0"),sQuery(id+"F8.wireOp",EDGE,"E79.0"),sQuery(id+"F8.wireOp",EDGE,"E80.0"),sQuery(id+"F8.wireOp",EDGE,"E81.0"),sQuery(id+"F8.wireOp",EDGE,"E82.0"),sQuery(id+"F8.wireOp",EDGE,"E83.0"),sQuery(id+"F8.wireOp",EDGE,"E84.0"),sQuery(id+"F8.wireOp",EDGE,"E85.0"),sQuery(id+"F8.wireOp",EDGE,"E86.0"),sQuery(id+"F8.wireOp",EDGE,"E87.0"),sQuery(id+"F8.wireOp",EDGE,"E88"),sQuery(id+"F8.wireOp",EDGE,"E89")])],"isStart":false});
            var sketch = newSketch(context, id + "F38", { "sketchPlane" : qUnion([Q0])});
            skLineSegment(sketch, "E130.top", {"start": v(-117.13, -118.12) * mm, "end": v(-48.93, -118.12) * mm});
            skLineSegment(sketch, "E130.left", {"start": v(-120.03, -138.12) * mm, "end": v(-120.03, -132.12) * mm});
            skLineSegment(sketch, "E130.right", {"start": v(-46.03, -138.12) * mm, "end": v(-46.03, -132.12) * mm});
            skLineSegment(sketch, "E131", {"start": v(-83.03, -106.12) * mm, "end": v(-83.03, -118.12) * mm, "construction": true});
            skLineSegment(sketch, "E132", {"start": v(-83.03, -118.12) * mm, "end": v(-83.03, -130.12) * mm, "construction": true});
            skLineSegment(sketch, "E133.bottom", {"start": v(-76.53, -134.12) * mm, "end": v(-54.03, -134.12) * mm});
            skLineSegment(sketch, "E133.top", {"start": v(-76.53, -122.12) * mm, "end": v(-54.03, -122.12) * mm});
            skLineSegment(sketch, "E133.left", {"start": v(-76.53, -134.12) * mm, "end": v(-76.53, -122.12) * mm});
            skLineSegment(sketch, "E133.right", {"start": v(-54.03, -134.12) * mm, "end": v(-54.03, -122.12) * mm});
            skLineSegment(sketch, "E134.bottom", {"start": v(-89.53, -134.12) * mm, "end": v(-112.03, -134.12) * mm});
            skLineSegment(sketch, "E134.top", {"start": v(-89.53, -122.12) * mm, "end": v(-112.03, -122.12) * mm});
            skLineSegment(sketch, "E134.left", {"start": v(-89.53, -134.12) * mm, "end": v(-89.53, -122.12) * mm});
            skLineSegment(sketch, "E134.right", {"start": v(-112.03, -134.12) * mm, "end": v(-112.03, -122.12) * mm});
            skLineSegment(sketch, "E135", {"start": v(-51.53, -128.12) * mm, "end": v(-79.03, -128.12) * mm, "construction": true});
            skLineSegment(sketch, "E136", {"start": v(-87.03, -128.12) * mm, "end": v(-114.53, -128.12) * mm, "construction": true});
            skLineSegment(sketch, "E137", {"start": v(-112.03, -128.12) * mm, "end": v(-89.53, -128.12) * mm, "construction": true});
            skLineSegment(sketch, "E138", {"start": v(-76.53, -128.12) * mm, "end": v(-54.03, -128.12) * mm, "construction": true});
            skLineSegment(sketch, "E139", {"start": v(-65.28, -128.12) * mm, "end": v(-65.28, -122.12) * mm, "construction": true});
            skLineSegment(sketch, "E140", {"start": v(-100.78, -128.12) * mm, "end": v(-100.78, -122.12) * mm, "construction": true});
            skLineSegment(sketch, "E141", {"start": v(-65.28, -128.12) * mm, "end": v(-65.28, -155.01) * mm, "construction": true});
            skLineSegment(sketch, "E142", {"start": v(-100.78, -128.12) * mm, "end": v(-100.78, -155.01) * mm, "construction": true});
            skPoint(sketch, "E142.endSnap0", {"position": v(-100.78, -128.12) * mm});
            skCircle(sketch, "E143", {"center": v(-114.53, -128.12) * mm, "radius": 1.5 * mm});
            skCircle(sketch, "E144", {"center": v(-87.03, -128.12) * mm, "radius": 1.5 * mm});
            skCircle(sketch, "E145", {"center": v(-79.03, -128.12) * mm, "radius": 1.5 * mm});
            skCircle(sketch, "E146", {"center": v(-51.53, -128.12) * mm, "radius": 1.5 * mm});
            skCircle(sketch, "E147", {"center": v(-95.53, -128.12) * mm, "radius": 6 * mm, "construction": true});
            skCircle(sketch, "E148", {"center": v(-70.53, -128.12) * mm, "radius": 6 * mm, "construction": true});
            skLineSegment(sketch, "E149", {"start": v(-95.53, -128.12) * mm, "end": v(-70.53, -128.12) * mm, "construction": true});
            skLineSegment(sketch, "E150", {"start": v(-83.03, -128.12) * mm, "end": v(-83.03, -134.12) * mm, "construction": true});
            skLineSegment(sketch, "E151", {"start": v(-120.03, -138.12) * mm, "end": v(-86.93, -138.12) * mm});
            skLineSegment(sketch, "E152.bottom", {"start": v(-120.03, -122.02) * mm, "end": v(-117.13, -122.02) * mm});
            skLineSegment(sketch, "E152.right", {"start": v(-117.13, -122.02) * mm, "end": v(-117.13, -118.12) * mm});
            skLineSegment(sketch, "E153.bottom", {"start": v(-46.03, -122.02) * mm, "end": v(-48.93, -122.02) * mm});
            skLineSegment(sketch, "E153.right", {"start": v(-48.93, -122.02) * mm, "end": v(-48.93, -118.12) * mm});
            skLineSegment(sketch, "E154.bottom", {"start": v(-120.03, -128.22) * mm, "end": v(-117.13, -128.22) * mm});
            skLineSegment(sketch, "E154.top", {"start": v(-120.03, -132.12) * mm, "end": v(-117.13, -132.12) * mm});
            skLineSegment(sketch, "E154.right", {"start": v(-117.13, -128.22) * mm, "end": v(-117.13, -132.12) * mm});
            skLineSegment(sketch, "E155.bottom", {"start": v(-46.03, -128.22) * mm, "end": v(-48.93, -128.22) * mm});
            skLineSegment(sketch, "E155.top", {"start": v(-46.03, -132.12) * mm, "end": v(-48.93, -132.12) * mm});
            skLineSegment(sketch, "E155.right", {"start": v(-48.93, -128.22) * mm, "end": v(-48.93, -132.12) * mm});
            skLineSegment(sketch, "E156.top", {"start": v(-86.93, -135.22) * mm, "end": v(-79.13, -135.22) * mm});
            skLineSegment(sketch, "E156.left", {"start": v(-86.93, -138.12) * mm, "end": v(-86.93, -135.22) * mm});
            skLineSegment(sketch, "E156.right", {"start": v(-79.13, -138.12) * mm, "end": v(-79.13, -135.22) * mm});
            skPoint(sketch, "E157.orphan", {"position": v(-120.03, -118.12) * mm});
            skPoint(sketch, "E158.orphan", {"position": v(-46.03, -118.12) * mm});
            skLineSegment(sketch, "E159.trimOffspring", {"start": v(-79.13, -138.12) * mm, "end": v(-46.03, -138.12) * mm});
            skLineSegment(sketch, "E160.trimOffspring", {"start": v(-120.03, -128.22) * mm, "end": v(-120.03, -122.02) * mm});
            skLineSegment(sketch, "E161.trimOffspring", {"start": v(-46.03, -128.22) * mm, "end": v(-46.03, -122.02) * mm});
            skSolve(sketch);
        }
        {
            var Q0;
            Q0=makeQuery(id+"F38.imprint","IMPRINT",FACE,{"disambiguationData":[TD([[makeQuery(id+"F38.imprint","IMPRINT",EDGE,{"derivedFrom":sQuery(id+"F38.wireOp",EDGE,"E130.top")}),-1.0]])]});
            extrude(context, id + "F39", {"entities" : qUnion([Q0]), "oppositeDirection" : true, "depth" : 3 * mm});
        }
        {
            var Q0;
            Q0=makeQuery(id+"F39.opExtrude","SWEPT_FACE",FACE,{"disambiguationData":[OSD([sQuery(id+"F38.wireOp",EDGE,"E151")])]});
            var sketch = newSketch(context, id + "F40", { "sketchPlane" : qUnion([Q0])});
            skLineSegment(sketch, "E162.bottom", {"start": v(-120.03, -50) * mm, "end": v(-46.03, -50) * mm});
            skLineSegment(sketch, "E162.top", {"start": v(-120.03, -35) * mm, "end": v(-93.53, -35) * mm});
            skLineSegment(sketch, "E162.left", {"start": v(-120.03, -50) * mm, "end": v(-120.03, -46.9) * mm});
            skLineSegment(sketch, "E162.right", {"start": v(-46.03, -50) * mm, "end": v(-46.03, -46.9) * mm});
            skLineSegment(sketch, "E163.top", {"start": v(-87.03, 6) * mm, "end": v(-79.03, 6) * mm});
            skLineSegment(sketch, "E163.left", {"start": v(-87.03, 3) * mm, "end": v(-87.03, 6) * mm});
            skLineSegment(sketch, "E163.right", {"start": v(-79.03, 3) * mm, "end": v(-79.03, 6) * mm});
            skLineSegment(sketch, "E164.0", {"start": v(-86.93, 6) * mm, "end": v(-79.13, 6) * mm, "construction": true});
            skLineSegment(sketch, "E165", {"start": v(-83.03, 6) * mm, "end": v(-83.03, 17.76) * mm, "construction": true});
            skLineSegment(sketch, "E166", {"start": v(-83.03, 6) * mm, "end": v(-83.03, -40.71) * mm, "construction": true});
            skPoint(sketch, "E163.bottom.start.orphan", {"position": v(-87.03, -40.71) * mm});
            skPoint(sketch, "E167.orphan", {"position": v(-79.03, -40.71) * mm});
            skLineSegment(sketch, "E168.trimOffspring", {"start": v(-72.53, -35) * mm, "end": v(-46.03, -35) * mm});
            skLineSegment(sketch, "E169.left", {"start": v(-93.53, 3) * mm, "end": v(-93.53, -35) * mm});
            skLineSegment(sketch, "E169.right", {"start": v(-72.53, 3) * mm, "end": v(-72.53, -35) * mm});
            skLineSegment(sketch, "E170", {"start": v(-93.53, 3) * mm, "end": v(-87.03, 3) * mm});
            skLineSegment(sketch, "E171.trimOffspring", {"start": v(-79.03, 3) * mm, "end": v(-72.53, 3) * mm});
            skLineSegment(sketch, "E172.bottom", {"start": v(-120.03, -38.1) * mm, "end": v(-117.13, -38.1) * mm});
            skLineSegment(sketch, "E172.top", {"start": v(-120.03, -46.9) * mm, "end": v(-117.13, -46.9) * mm});
            skLineSegment(sketch, "E172.right", {"start": v(-117.13, -38.1) * mm, "end": v(-117.13, -46.9) * mm});
            skLineSegment(sketch, "E173.bottom", {"start": v(-46.03, -38.1) * mm, "end": v(-48.93, -38.1) * mm});
            skLineSegment(sketch, "E173.top", {"start": v(-46.03, -46.9) * mm, "end": v(-48.93, -46.9) * mm});
            skLineSegment(sketch, "E173.right", {"start": v(-48.93, -38.1) * mm, "end": v(-48.93, -46.9) * mm});
            skLineSegment(sketch, "E174.trimOffspring", {"start": v(-46.03, -38.1) * mm, "end": v(-46.03, -35) * mm});
            skLineSegment(sketch, "E175.trimOffspring", {"start": v(-120.03, -38.1) * mm, "end": v(-120.03, -35) * mm});
            skSolve(sketch);
        }
        {
            var Q0;
            Q0=makeQuery(id+"F40.imprint","IMPRINT",FACE,{"disambiguationData":[TD([[makeQuery(id+"F40.imprint","IMPRINT",EDGE,{"derivedFrom":sQuery(id+"F40.wireOp",EDGE,"E162.bottom")}),1.0]])]});
            extrude(context, id + "F41", {"entities" : qUnion([Q0]), "oppositeDirection" : true, "depth" : 3 * mm});
        }
        {
            var Q0;
            Q0=makeQuery(id+"F41.opExtrude","SWEPT_EDGE",EDGE,{"disambiguationData":[OSD([sQuery(id+"F40.wireOp",EDGE,"E162.top"),sQuery(id+"F40.wireOp",EDGE,"E169.left")])]});
            var Q1;
            Q1=makeQuery(id+"F41.opExtrude","SWEPT_EDGE",EDGE,{"disambiguationData":[OSD([sQuery(id+"F40.wireOp",EDGE,"E168.trimOffspring"),sQuery(id+"F40.wireOp",EDGE,"E169.right")])]});
            fillet(context, id + "F42", {"entities" : qUnion([Q0, Q1]), "radius" : 15 * mm, "tangentPropagation" : true, "allowEdgeOverflow" : false});
        }
        {
            var Q0;
            Q0=makeQuery(id+"F39.opExtrude","SWEPT_FACE",FACE,{"disambiguationData":[OSD([sQuery(id+"F38.wireOp",EDGE,"E160.trimOffspring")])]});
            var sketch = newSketch(context, id + "F43", { "sketchPlane" : qUnion([Q0])});
            skLineSegment(sketch, "E176.top", {"start": v(135.12, -50) * mm, "end": v(118.12, -50) * mm});
            skLineSegment(sketch, "E176.left", {"start": v(138.12, 3) * mm, "end": v(138.12, -35) * mm});
            skLineSegment(sketch, "E176.right", {"start": v(106.12, -35) * mm, "end": v(106.12, -50) * mm});
            skLineSegment(sketch, "E177", {"start": v(118.12, 3) * mm, "end": v(118.12, -35) * mm});
            skLineSegment(sketch, "E178", {"start": v(118.12, -35) * mm, "end": v(106.12, -35) * mm});
            skLineSegment(sketch, "E179.right", {"start": v(122.12, 3) * mm, "end": v(122.12, 6) * mm});
            skLineSegment(sketch, "E180.left", {"start": v(128.17, 6) * mm, "end": v(128.17, 3) * mm});
            skLineSegment(sketch, "E180.right", {"start": v(132.17, 6) * mm, "end": v(132.17, 3) * mm});
            skPoint(sketch, "E181.orphan", {"position": v(118.12, 6) * mm});
            skLineSegment(sketch, "E182.top", {"start": v(138.12, -47) * mm, "end": v(135.12, -47) * mm});
            skLineSegment(sketch, "E182.right", {"start": v(135.12, -50) * mm, "end": v(135.12, -47) * mm});
            skLineSegment(sketch, "E183.bottom", {"start": v(138.12, -35) * mm, "end": v(135.12, -35) * mm});
            skLineSegment(sketch, "E183.top", {"start": v(138.12, -38) * mm, "end": v(135.12, -38) * mm});
            skLineSegment(sketch, "E183.right", {"start": v(135.12, -35) * mm, "end": v(135.12, -38) * mm});
            skLineSegment(sketch, "E184.trimOffspring", {"start": v(138.12, -38) * mm, "end": v(138.12, -47) * mm});
            skLineSegment(sketch, "E185", {"start": v(110.12, -47) * mm, "end": v(110.12, -50) * mm});
            skPoint(sketch, "E186.orphan", {"position": v(118.12, -47) * mm});
            skLineSegment(sketch, "E187", {"start": v(110.12, -47) * mm, "end": v(118.12, -47) * mm});
            skLineSegment(sketch, "E188", {"start": v(118.12, -47) * mm, "end": v(118.12, -50) * mm});
            skLineSegment(sketch, "E189.trimOffspring", {"start": v(110.12, -50) * mm, "end": v(106.12, -50) * mm});
            skLineSegment(sketch, "E190", {"start": v(122.12, 6) * mm, "end": v(118.12, 6) * mm});
            skLineSegment(sketch, "E191", {"start": v(118.12, 6) * mm, "end": v(118.12, 3) * mm});
            skLineSegment(sketch, "E192", {"start": v(128.17, 6) * mm, "end": v(132.17, 6) * mm});
            skLineSegment(sketch, "E193", {"start": v(128.17, 3) * mm, "end": v(122.12, 3) * mm});
            skLineSegment(sketch, "E194", {"start": v(132.17, 3) * mm, "end": v(138.12, 3) * mm});
            skPoint(sketch, "E176.bottom.start.orphan", {"position": v(138.12, 6) * mm});
            skSolve(sketch);
        }
        {
            var Q0;
            Q0 = qSketchRegion(id + "F43", true);
            extrude(context, id + "F44", {"entities" : qUnion([Q0]), "oppositeDirection" : true, "depth" : 3 * mm});
        }
        {
            var Q0;
            Q0=makeQuery(id+"F29.opPattern","COPY",FACE,{"derivedFrom":makeQuery(id+"F1.opExtrude","CAP_FACE",FACE,{"disambiguationData":[OSD([sQuery(id+"F0.wireOp",EDGE,"E0.0.0"),sQuery(id+"F0.wireOp",EDGE,"E0.0.2"),sQuery(id+"F0.wireOp",EDGE,"E0.0.4"),sQuery(id+"F0.wireOp",EDGE,"E0.0.6"),sQuery(id+"F0.wireOp",EDGE,"E1.0"),sQuery(id+"F0.wireOp",EDGE,"E2.0"),sQuery(id+"F0.wireOp",EDGE,"E3.0"),sQuery(id+"F0.wireOp",EDGE,"E4.0")])],"isStart":false}),"instanceName":"1"});
            var sketch = newSketch(context, id + "F45", { "sketchPlane" : qUnion([Q0])});
            skLineSegment(sketch, "E195.0", {"start": v(-117.03, 110.12) * mm, "end": v(-117.03, 106.12) * mm});
            skLineSegment(sketch, "E196.0", {"start": v(-117.03, 106.12) * mm, "end": v(-120.03, 106.12) * mm});
            skLineSegment(sketch, "E197.0", {"start": v(-120.03, 110.12) * mm, "end": v(-120.03, 106.12) * mm});
            skLineSegment(sketch, "E198.0", {"start": v(-117.03, 110.12) * mm, "end": v(-120.03, 110.12) * mm});
            skLineSegment(sketch, "E199", {"start": v(-83.03, 106.12) * mm, "end": v(-83.03, 118.12) * mm, "construction": true});
            skLineSegment(sketch, "E200.MirrorCS", {"start": v(-49.03, 110.12) * mm, "end": v(-46.03, 110.12) * mm});
            skLineSegment(sketch, "E201.MirrorCS", {"start": v(-49.03, 106.12) * mm, "end": v(-46.03, 106.12) * mm});
            skLineSegment(sketch, "E202.MirrorCS", {"start": v(-46.03, 110.12) * mm, "end": v(-46.03, 106.12) * mm});
            skLineSegment(sketch, "E203.MirrorCS", {"start": v(-49.03, 110.12) * mm, "end": v(-49.03, 106.12) * mm});
            skSolve(sketch);
        }
        {
            var Q0;
            Q0 = qSketchRegion(id + "F45", true);
            extrude(context, id + "F46", {"entities" : qUnion([Q0]), "operationType" : NewBodyOperationType.REMOVE, "oppositeDirection" : true, "depth" : 3 * mm});
        }
        {
            var Q0;
            Q0=makeQuery(id+"F37.opExtrude","SWEPT_BODY",BODY,{"disambiguationData":[OSD([sQuery(id+"F36.wireOp",EDGE,"E123.0"),sQuery(id+"F36.wireOp",EDGE,"E128.0.startCap"),sQuery(id+"F36.wireOp",EDGE,"E128.0.endCap"),sQuery(id+"F36.wireOp",EDGE,"E128.0.left"),sQuery(id+"F36.wireOp",EDGE,"E128.0.right"),sQuery(id+"F36.wireOp",EDGE,"E129")])]});
            var Q1;
            Q1=makeQuery(id+"F33.opExtrude","SWEPT_BODY",BODY,{"disambiguationData":[OSD([sQuery(id+"F32.wireOp",EDGE,"E113.bottom"),sQuery(id+"F32.wireOp",EDGE,"E113.top"),sQuery(id+"F32.wireOp",EDGE,"E113.left"),sQuery(id+"F32.wireOp",EDGE,"E113.right"),sQuery(id+"F32.wireOp",EDGE,"E114"),sQuery(id+"F32.wireOp",EDGE,"E115"),sQuery(id+"F32.wireOp",EDGE,"E118.bottom"),sQuery(id+"F32.wireOp",EDGE,"E118.top"),sQuery(id+"F32.wireOp",EDGE,"E118.left"),sQuery(id+"F32.wireOp",EDGE,"E118.right")])]});
            var Q2;
            Q2=makeQuery(id+"F44.opExtrude","SWEPT_BODY",BODY,{"disambiguationData":[OSD([sQuery(id+"F43.wireOp",EDGE,"E176.top"),sQuery(id+"F43.wireOp",EDGE,"E176.left"),sQuery(id+"F43.wireOp",EDGE,"E176.right"),sQuery(id+"F43.wireOp",EDGE,"E177"),sQuery(id+"F43.wireOp",EDGE,"E178"),sQuery(id+"F43.wireOp",EDGE,"E179.right"),sQuery(id+"F43.wireOp",EDGE,"E180.left"),sQuery(id+"F43.wireOp",EDGE,"E180.right"),sQuery(id+"F43.wireOp",EDGE,"E182.top"),sQuery(id+"F43.wireOp",EDGE,"E182.right"),sQuery(id+"F43.wireOp",EDGE,"E183.bottom"),sQuery(id+"F43.wireOp",EDGE,"E183.top"),sQuery(id+"F43.wireOp",EDGE,"E183.right"),sQuery(id+"F43.wireOp",EDGE,"E184.trimOffspring"),sQuery(id+"F43.wireOp",EDGE,"E185"),sQuery(id+"F43.wireOp",EDGE,"E187"),sQuery(id+"F43.wireOp",EDGE,"E188"),sQuery(id+"F43.wireOp",EDGE,"E189.trimOffspring"),sQuery(id+"F43.wireOp",EDGE,"E190"),sQuery(id+"F43.wireOp",EDGE,"E191"),sQuery(id+"F43.wireOp",EDGE,"E192"),sQuery(id+"F43.wireOp",EDGE,"E193"),sQuery(id+"F43.wireOp",EDGE,"E194")])]});
            var Q3;
            Q3=qCreatedBy(id+"F14.planeOp",FACE);
            mirror(context, id + "F47", {"entities" : qUnion([Q0, Q1, Q2]), "mirrorPlane" : qUnion([Q3])});
        }
        {
            var Q0;
            Q0=makeQuery(id+"F33.opExtrude","SWEPT_EDGE",EDGE,{"disambiguationData":[OSD([sQuery(id+"F32.wireOp",EDGE,"E118.bottom"),sQuery(id+"F32.wireOp",EDGE,"E118.left")])]});
            var Q1;
            Q1=makeQuery(id+"F33.opExtrude","SWEPT_EDGE",EDGE,{"disambiguationData":[OSD([sQuery(id+"F32.wireOp",EDGE,"E118.bottom"),sQuery(id+"F32.wireOp",EDGE,"E118.right")])]});
            fillet(context, id + "F48", {"entities" : qUnion([Q0, Q1]), "radius" : 3 * mm, "tangentPropagation" : true, "allowEdgeOverflow" : false});
        }
    });
